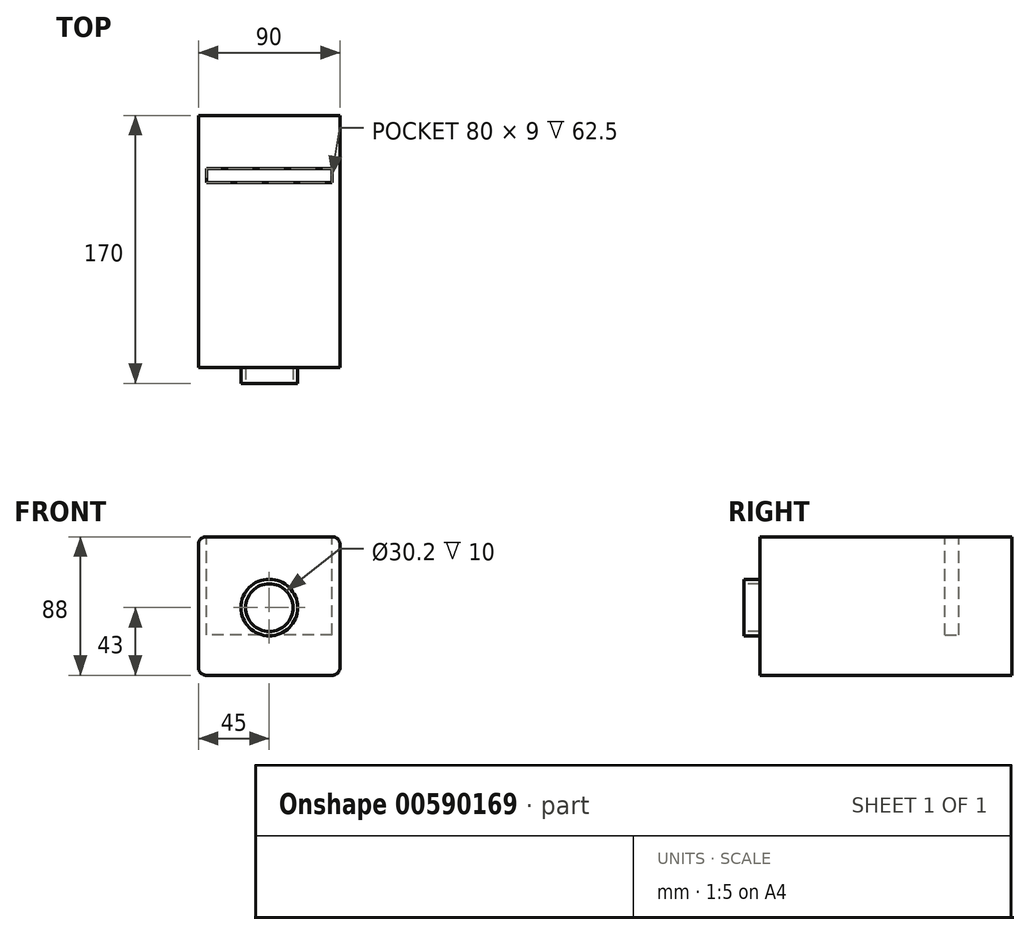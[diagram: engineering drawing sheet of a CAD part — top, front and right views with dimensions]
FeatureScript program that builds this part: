
annotation { "Feature Type Name" : "Feature", "Feature Type Description" : "" }
export const myFeature = defineFeature(function(context is Context, id is Id, definition is map)
    precondition{}
    {
        {
            var Q0;
            Q0=qCreatedBy(makeId("Top.planeOp"),FACE);
            var sketch = newSketch(context, id + "F0", { "sketchPlane" : qUnion([Q0])});
            skLineSegment(sketch, "E0.bottom", {"start": v(45, -80) * mm, "end": v(-45, -80) * mm});
            skLineSegment(sketch, "E0.top", {"start": v(45, 80) * mm, "end": v(-45, 80) * mm});
            skLineSegment(sketch, "E0.left", {"start": v(45, -80) * mm, "end": v(45, 80) * mm});
            skLineSegment(sketch, "E0.right", {"start": v(-45, -80) * mm, "end": v(-45, 80) * mm});
            skPoint(sketch, "E0.middle", {"position": v(0, 0) * mm});
            skSolve(sketch);
        }
        {
            var Q0;
            Q0=makeQuery(id+"F0.imprint","IMPRINT",FACE,{"disambiguationData":[TD([[makeQuery(id+"F0.imprint","IMPRINT",EDGE,{"derivedFrom":sQuery(id+"F0.wireOp",EDGE,"E0.bottom")}),-1.0]])]});
            extrude(context, id + "F1", {"entities" : qUnion([Q0]), "depth" : 88 * mm, "offsetDistance" : 25 * mm});
        }
        {
            var Q0;
            Q0=makeQuery(id+"F1.opExtrude","CAP_FACE",FACE,{"disambiguationData":[OSD([sQuery(id+"F0.wireOp",EDGE,"E0.bottom"),sQuery(id+"F0.wireOp",EDGE,"E0.top"),sQuery(id+"F0.wireOp",EDGE,"E0.left"),sQuery(id+"F0.wireOp",EDGE,"E0.right")])],"isStart":false});
            var sketch = newSketch(context, id + "F2", { "sketchPlane" : qUnion([Q0])});
            skLineSegment(sketch, "E1.bottom", {"start": v(40, 37.46) * mm, "end": v(-40, 37.46) * mm});
            skLineSegment(sketch, "E1.top", {"start": v(40, 46.46) * mm, "end": v(-40, 46.46) * mm});
            skLineSegment(sketch, "E1.left", {"start": v(40, 37.46) * mm, "end": v(40, 46.46) * mm});
            skLineSegment(sketch, "E1.right", {"start": v(-40, 37.46) * mm, "end": v(-40, 46.46) * mm});
            skPoint(sketch, "E1.middle", {"position": v(0, 41.96) * mm});
            skSolve(sketch);
        }
        {
            var Q0;
            Q0=makeQuery(id+"F2.imprint","IMPRINT",FACE,{"disambiguationData":[TD([[makeQuery(id+"F2.imprint","IMPRINT",EDGE,{"derivedFrom":sQuery(id+"F2.wireOp",EDGE,"E1.bottom")}),-1.0]])]});
            extrude(context, id + "F3", {"entities" : qUnion([Q0]), "operationType" : NewBodyOperationType.REMOVE, "endBound" : BoundingType.SYMMETRIC, "oppositeDirection" : true, "depth" : 25 * mm, "offsetDistance" : 25 * mm});
        }
        {
            var Q0;
            Q0=makeQuery(id+"F3.boolean.opBoolean","COPY",FACE,{"derivedFrom":makeQuery(id+"F3.opExtrude","CAP_FACE",FACE,{"disambiguationData":[OSD([sQuery(id+"F2.wireOp",EDGE,"E1.bottom"),sQuery(id+"F2.wireOp",EDGE,"E1.top"),sQuery(id+"F2.wireOp",EDGE,"E1.left"),sQuery(id+"F2.wireOp",EDGE,"E1.right")])],"isStart":false})});
            extrude(context, id + "F4", {"entities" : qUnion([Q0]), "operationType" : NewBodyOperationType.REMOVE, "oppositeDirection" : true, "depth" : 50 * mm, "offsetDistance" : 25 * mm});
        }
        {
            var Q0;
            Q0=makeQuery(id+"F1.opExtrude","SWEPT_FACE",FACE,{"disambiguationData":[OSD([sQuery(id+"F0.wireOp",EDGE,"E0.bottom")])]});
            var sketch = newSketch(context, id + "F5", { "sketchPlane" : qUnion([Q0])});
            skCircle(sketch, "E2", {"center": v(0, 43) * mm, "radius": 17.99 * mm});
            skSolve(sketch);
        }
        {
            var Q0;
            Q0 = qSketchRegion(id + "F5", true);
            extrude(context, id + "F6", {"entities" : qUnion([Q0]), "operationType" : NewBodyOperationType.ADD, "depth" : 10 * mm, "offsetDistance" : 25 * mm});
        }
        {
            var Q0;
            Q0=makeQuery(id+"F6.opExtrude","CAP_FACE",FACE,{"disambiguationData":[OSD([sQuery(id+"F5.wireOp",EDGE,"E2")])],"isStart":false});
            var sketch = newSketch(context, id + "F7", { "sketchPlane" : qUnion([Q0])});
            skCircle(sketch, "E3", {"center": v(0, 43) * mm, "radius": 15.1 * mm});
            skSolve(sketch);
        }
        {
            var Q0;
            Q0 = qSketchRegion(id + "F7", true);
            extrude(context, id + "F8", {"entities" : qUnion([Q0]), "operationType" : NewBodyOperationType.REMOVE, "oppositeDirection" : true, "depth" : 10 * mm, "offsetDistance" : 25 * mm});
        }
        {
            var Q0;
            Q0=makeQuery(id+"F1.opExtrude","CAP_EDGE",EDGE,{"disambiguationData":[OSD([sQuery(id+"F0.wireOp",EDGE,"E0.right")])],"isStart":false});
            var Q1;
            Q1=makeQuery(id+"F1.opExtrude","CAP_EDGE",EDGE,{"disambiguationData":[OSD([sQuery(id+"F0.wireOp",EDGE,"E0.left")])],"isStart":false});
            var Q2;
            Q2=makeQuery(id+"F1.opExtrude","CAP_EDGE",EDGE,{"disambiguationData":[OSD([sQuery(id+"F0.wireOp",EDGE,"E0.left")])],"isStart":true});
            var Q3;
            Q3=makeQuery(id+"F1.opExtrude","CAP_EDGE",EDGE,{"disambiguationData":[OSD([sQuery(id+"F0.wireOp",EDGE,"E0.right")])],"isStart":true});
            fillet(context, id + "F9", {"entities" : qUnion([Q0, Q1, Q2, Q3]), "radius" : 5 * mm, "tangentPropagation" : true, "allowEdgeOverflow" : false});
        }
    });
